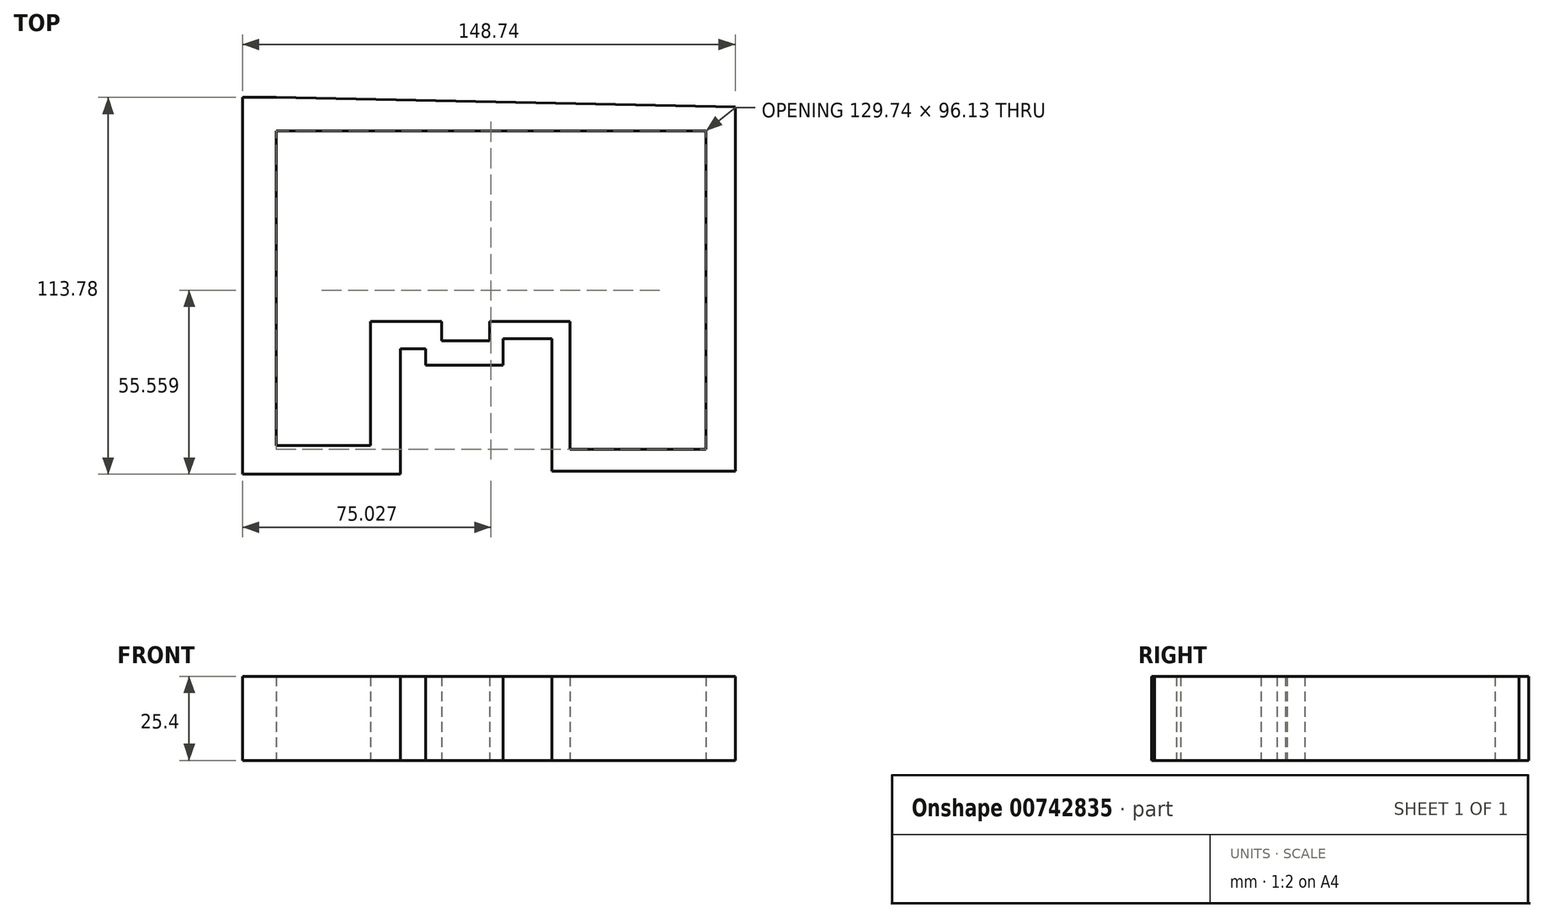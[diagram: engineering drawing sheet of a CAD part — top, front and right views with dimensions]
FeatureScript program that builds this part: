
annotation { "Feature Type Name" : "Feature", "Feature Type Description" : "" }
export const myFeature = defineFeature(function(context is Context, id is Id, definition is map)
    precondition{}
    {
        {
            var Q0;
            Q0=qCreatedBy(makeId("Top.planeOp"),FACE);
            var sketch = newSketch(context, id + "F0", { "sketchPlane" : qUnion([Q0])});
            skLineSegment(sketch, "E0.bottom", {"start": v(-68.5, 46.67) * mm, "end": v(61.24, 46.67) * mm});
            skLineSegment(sketch, "E0.left", {"start": v(-68.5, 46.67) * mm, "end": v(-68.5, -10.77) * mm});
            skLineSegment(sketch, "E0.right", {"start": v(61.24, 46.67) * mm, "end": v(61.24, -10.77) * mm});
            skLineSegment(sketch, "E1.top", {"start": v(-68.5, -48.28) * mm, "end": v(-39.96, -48.28) * mm});
            skLineSegment(sketch, "E1.left", {"start": v(-68.5, -10.77) * mm, "end": v(-68.5, -48.28) * mm});
            skLineSegment(sketch, "E1.right", {"start": v(-39.96, -10.77) * mm, "end": v(-39.96, -48.28) * mm});
            skLineSegment(sketch, "E2.top", {"start": v(61.24, -49.46) * mm, "end": v(20.21, -49.46) * mm});
            skLineSegment(sketch, "E2.left", {"start": v(61.24, -10.77) * mm, "end": v(61.24, -49.46) * mm});
            skLineSegment(sketch, "E2.right", {"start": v(20.21, -10.77) * mm, "end": v(20.21, -49.46) * mm});
            skLineSegment(sketch, "E3.top", {"start": v(-18.47, -16.63) * mm, "end": v(-4.01, -16.63) * mm});
            skLineSegment(sketch, "E3.left", {"start": v(-18.47, -10.77) * mm, "end": v(-18.47, -16.63) * mm});
            skLineSegment(sketch, "E3.right", {"start": v(-4.01, -10.77) * mm, "end": v(-4.01, -16.63) * mm});
            skLineSegment(sketch, "E4", {"start": v(-39.96, -10.77) * mm, "end": v(-18.47, -10.77) * mm});
            skLineSegment(sketch, "E5", {"start": v(20.21, -10.77) * mm, "end": v(-4.01, -10.77) * mm});
            skLineSegment(sketch, "E6", {"start": v(-68.5, -10.77) * mm, "end": v(-49.73, -10.77) * mm});
            skLineSegment(sketch, "E7", {"start": v(61.24, -10.77) * mm, "end": v(31.55, -10.77) * mm});
            skLineSegment(sketch, "E8", {"start": v(26.47, 46.67) * mm, "end": v(26.47, 15.8) * mm});
            skLineSegment(sketch, "E9", {"start": v(61.24, 15.8) * mm, "end": v(38.97, 15.8) * mm});
            skLineSegment(sketch, "E10", {"start": v(-2.84, 15.8) * mm, "end": v(-2.84, 46.67) * mm});
            skLineSegment(sketch, "E11", {"start": v(-2.84, 15.8) * mm, "end": v(15.92, 15.8) * mm});
            skLineSegment(sketch, "E12.bottom", {"start": v(-57.94, 38.86) * mm, "end": v(-38.4, 38.86) * mm});
            skLineSegment(sketch, "E12.top", {"start": v(-57.94, 28.7) * mm, "end": v(-38.4, 28.7) * mm});
            skLineSegment(sketch, "E12.left", {"start": v(-57.94, 38.86) * mm, "end": v(-57.94, 28.7) * mm});
            skLineSegment(sketch, "E12.right", {"start": v(-38.4, 38.86) * mm, "end": v(-38.4, 28.7) * mm});
            skLineSegment(sketch, "E13", {"start": v(-68.5, 46.67) * mm, "end": v(-68.5, 56.83) * mm});
            skLineSegment(sketch, "E14", {"start": v(-68.5, 56.83) * mm, "end": v(-78.65, 56.83) * mm});
            skLineSegment(sketch, "E15", {"start": v(-78.65, 56.83) * mm, "end": v(-78.65, -56.95) * mm});
            skLineSegment(sketch, "E16", {"start": v(-78.65, -56.95) * mm, "end": v(-31, -56.95) * mm});
            skLineSegment(sketch, "E17", {"start": v(-31, -56.95) * mm, "end": v(-31, -19.09) * mm});
            skLineSegment(sketch, "E18", {"start": v(-31, -19.09) * mm, "end": v(-23.36, -19.09) * mm});
            skLineSegment(sketch, "E19", {"start": v(-23.36, -19.09) * mm, "end": v(-23.36, -23.97) * mm});
            skLineSegment(sketch, "E20", {"start": v(-23.36, -23.97) * mm, "end": v(0, -23.97) * mm});
            skLineSegment(sketch, "E21", {"start": v(0, -23.97) * mm, "end": v(0, -16.03) * mm});
            skLineSegment(sketch, "E22", {"start": v(0, -16.03) * mm, "end": v(14.81, -16.03) * mm});
            skLineSegment(sketch, "E23", {"start": v(14.81, -16.03) * mm, "end": v(14.81, -56.04) * mm});
            skLineSegment(sketch, "E24", {"start": v(14.81, -56.04) * mm, "end": v(70.09, -56.04) * mm});
            skLineSegment(sketch, "E25", {"start": v(70.09, -56.04) * mm, "end": v(70.09, 53.9) * mm});
            skLineSegment(sketch, "E26", {"start": v(70.09, 53.9) * mm, "end": v(-68.5, 56.83) * mm});
            skSolve(sketch);
        }
        {
            var Q0;
            {var subQ1=sQuery(id+"F0.wireOp",EDGE,"E0.left");Q0=makeQuery(id+"F0.imprint","IMPRINT",FACE,{"disambiguationData":[TD([[makeQuery(id+"F0.imprint","IMPRINT",EDGE,{"derivedFrom":subQ1}),-1.0]])]});}
            extrude(context, id + "F1", {"entities" : qUnion([Q0]), "depth" : 25.4 * mm, "offsetDistance" : 25.4 * mm});
        }
    });
